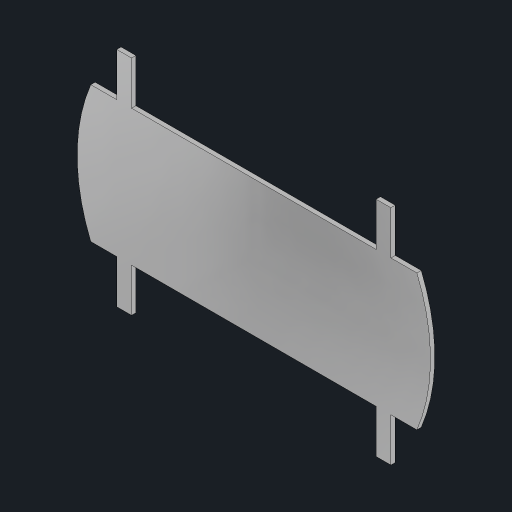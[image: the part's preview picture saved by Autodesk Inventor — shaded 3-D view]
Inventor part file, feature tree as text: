
AUTODESK INVENTOR PART (.ipt)
format: ipt  version: 2023.2 (Build 272271030, 271C)  size: 123,392 bytes
history: native  units: mm
features: extrude x1, sketch x1
ambient origin geometry x8: Origin, YZ Plane, XZ Plane, XY Plane, X Axis, Y Axis, Z Axis, Center Point
bodies: Solid1 (feature_tree)
feature tree (2):
  extrude  "Extrusion1"  Depth=50.0mm
  sketch  "Sketch1"  dims[d0=130.0mm d1=50.0mm d2=90.0mm d4=16.0mm d5=1.6mm d6=0.0mm]
